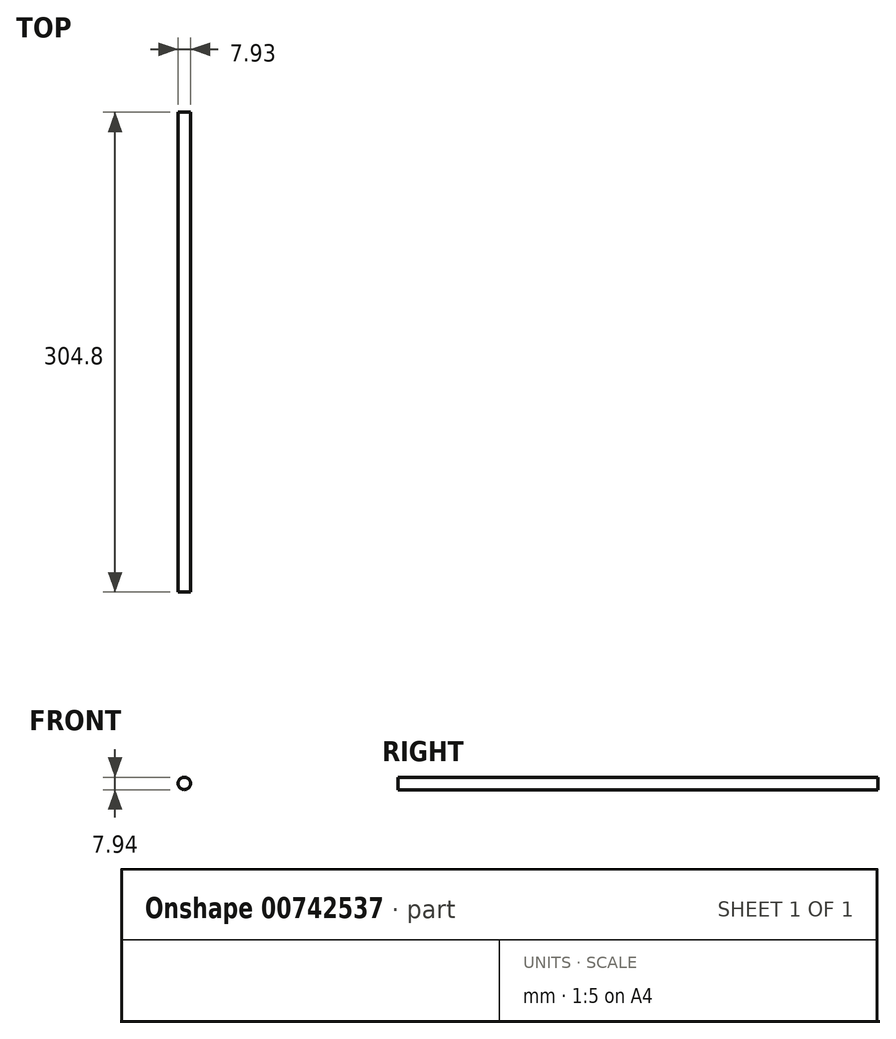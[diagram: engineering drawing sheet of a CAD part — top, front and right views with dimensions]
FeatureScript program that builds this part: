
annotation { "Feature Type Name" : "Feature", "Feature Type Description" : "" }
export const myFeature = defineFeature(function(context is Context, id is Id, definition is map)
    precondition{}
    {
        {
            var Q0;
            Q0=qCreatedBy(makeId("Front.planeOp"),FACE);
            var sketch = newSketch(context, id + "F0", { "sketchPlane" : qUnion([Q0])});
            skCircle(sketch, "E0", {"center": v(-58.8, 42.56) * mm, "radius": 3.97 * mm});
            skSolve(sketch);
        }
        {
            var Q0;
            Q0=makeQuery(id+"F0.imprint","IMPRINT",FACE,{"disambiguationData":[TD([[makeQuery(id+"F0.imprint","IMPRINT",EDGE,{"derivedFrom":sQuery(id+"F0.wireOp",EDGE,"E0")}),1.0]])]});
            extrude(context, id + "F1", {"entities" : qUnion([Q0]), "depth" : 304.8 * mm, "offsetDistance" : 25.4 * mm});
        }
    });
